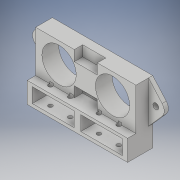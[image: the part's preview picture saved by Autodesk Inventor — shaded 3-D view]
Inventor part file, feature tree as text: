
AUTODESK INVENTOR PART (.ipt)
format: ipt  version: 2019 (Build 230136000, 136)  size: 216,576 bytes
history: native  units: mm
features: sketch x7, extrude x5, projected_geometry x3, hole x2, other x1
ambient origin geometry x8: Origin, YZ Plane, XZ Plane, XY Plane, X Axis, Y Axis, Z Axis, Center Point
bodies: Body1 (feature_tree)
feature tree (18):
  other  "Твердое тело1"
  extrude  "Выдавливание1"  Depth=20.0mm
  extrude  "Выдавливание2"  Depth=48.0mm
  extrude  "Выдавливание3"  Depth=4.0mm
  extrude  "Выдавливание4"  Depth=55.0mm
  hole  "Отверстие1"  [1 undecoded]
  extrude  "Выдавливание5"  Depth=6.0mm TaperAngle=0.0deg
  hole  "Отверстие2"  [1 undecoded]
  sketch  "Эскиз1"
  sketch  "Эскиз2"
  sketch  "Эскиз3"
  sketch  "Эскиз4"
  sketch  "Эскиз5"
  sketch  "Эскиз6"
  sketch  "Эскиз7"
  projected_geometry  "Спроецированная петля1"
  projected_geometry  "Спроецированная петля2"
  projected_geometry  "Спроецированная петля3"
note: 2 required parameter values undecoded (feature->parameter linkage not recoverable at this tier; creation-order binding heuristic only, values carry confidence <= 0.55)
